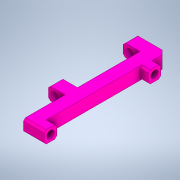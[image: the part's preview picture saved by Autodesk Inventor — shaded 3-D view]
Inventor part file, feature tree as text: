
AUTODESK INVENTOR PART (.ipt)
format: ipt  version: 2020 (Build 240168000, 168)  size: 180,224 bytes
history: native  units: mm
features: extrude x3, chamfer x3, sketch x2
ambient origin geometry x8: Origin, YZ Plane, XZ Plane, XY Plane, X Axis, Y Axis, Z Axis, Center Point
bodies: Solid1 (feature_tree)
feature tree (8):
  extrude  "Extrusion1"  Depth=6.0mm
  extrude  "Extrusion4"  Depth=6.0mm TaperAngle=0.0deg
  chamfer  "Chamfer2"  Distance=6.0mm
  chamfer  "Chamfer3"  Distance=20.0mm
  sketch  "Sketch5"  dims[d4=4.0mm d6=6.0mm d7=0.0mm d19=6.0mm d20=20.0mm d21=6.0mm d22=8.0mm d23=30.0mm d24=3.5mm d25=0.0mm d26=0.0mm d27=1.0mm d28=2.0mm d29=45.0deg d30=2.0mm d31=2.0mm d32=45.0deg d33=3.5mm d34=1.0mm d35=2.0mm d36=45.0deg d37=0.0mm d38=0.0mm]
  chamfer  "Chamfer4"  Distance=6.0mm
  extrude  "Extrusion5"  Depth=8.0mm
  sketch  "Sketch4"  dims[d2=50.0mm d3=6.0mm]
